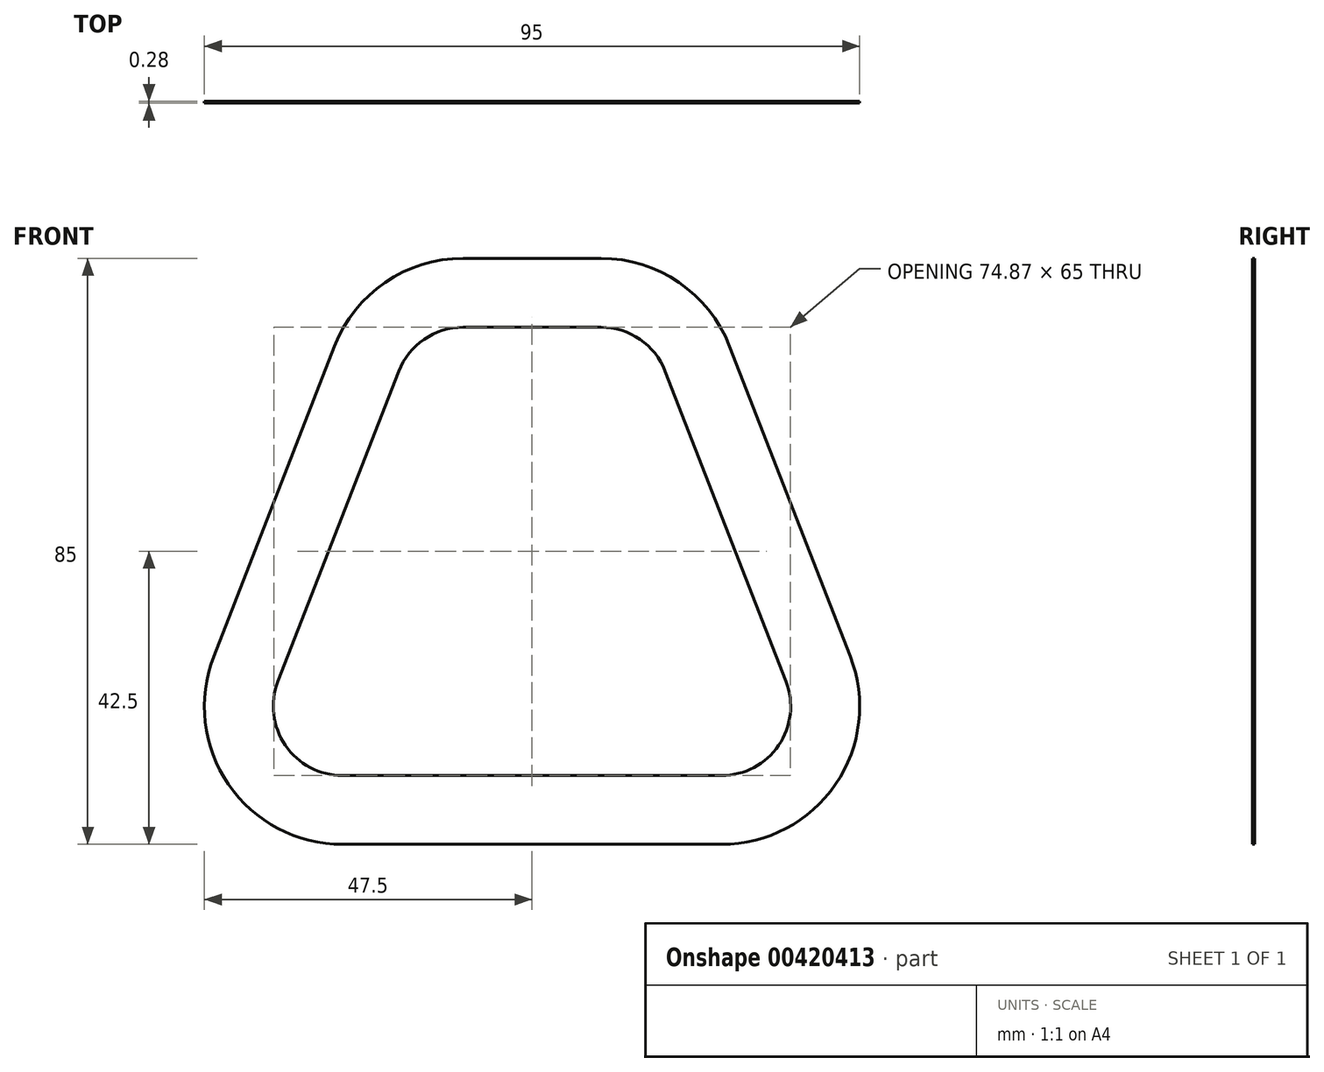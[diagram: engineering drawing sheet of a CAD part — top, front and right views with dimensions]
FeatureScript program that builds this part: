
annotation { "Feature Type Name" : "Feature", "Feature Type Description" : "" }
export const myFeature = defineFeature(function(context is Context, id is Id, definition is map)
    precondition{}
    {
        {
            var Q0;
            Q0=qCreatedBy(makeId("Front.planeOp"),FACE);
            var sketch = newSketch(context, id + "F0", { "sketchPlane" : qUnion([Q0])});
            skLineSegment(sketch, "E0", {"start": v(0, 0) * mm, "end": v(0, 20) * mm, "construction": true});
            skLineSegment(sketch, "E1", {"start": v(0, 20) * mm, "end": v(10, 20) * mm});
            skLineSegment(sketch, "E2", {"start": v(10, 20) * mm, "end": v(27.5, -25) * mm});
            skLineSegment(sketch, "E3", {"start": v(27.5, -25) * mm, "end": v(6.93, -25) * mm});
            skLineSegment(sketch, "E4", {"start": v(6.93, -25) * mm, "end": v(0, -13) * mm});
            skLineSegment(sketch, "E5", {"start": v(27.5, -25) * mm, "end": v(27.5, 20) * mm, "construction": true});
            skLineSegment(sketch, "E6", {"start": v(6.93, -25) * mm, "end": v(6.93, -13) * mm, "construction": true});
            skPoint(sketch, "E7.visualSharp", {"position": v(10, 20) * mm});
            skPoint(sketch, "E8.visualSharp", {"position": v(27.5, -25) * mm});
            skLineSegment(sketch, "E9.MirrorCS", {"start": v(0, 20) * mm, "end": v(-10, 20) * mm});
            skPoint(sketch, "E10.MirrorP", {"position": v(-27.5, -25) * mm});
            skLineSegment(sketch, "E11.MirrorCS", {"start": v(-10, 20) * mm, "end": v(-27.5, -25) * mm});
            skLineSegment(sketch, "E12.MirrorCS", {"start": v(-27.5, -25) * mm, "end": v(-6.93, -25) * mm});
            skLineSegment(sketch, "E13.MirrorCS", {"start": v(-27.5, -25) * mm, "end": v(-27.5, 20) * mm, "construction": true});
            skLineSegment(sketch, "E14.MirrorCS", {"start": v(-6.93, -25) * mm, "end": v(0, -13) * mm});
            skLineSegment(sketch, "E15.MirrorCS", {"start": v(-6.93, -25) * mm, "end": v(-6.93, -13) * mm, "construction": true});
            skLineSegment(sketch, "E16.0", {"start": v(0, 30) * mm, "end": v(10, 30) * mm});
            skLineSegment(sketch, "E16.1", {"start": v(0, 30) * mm, "end": v(-10, 30) * mm});
            skLineSegment(sketch, "E16.2", {"start": v(19.32, 23.62) * mm, "end": v(36.82, -21.38) * mm});
            skLineSegment(sketch, "E16.3", {"start": v(-19.32, 23.62) * mm, "end": v(-36.82, -21.38) * mm});
            skLineSegment(sketch, "E16.7", {"start": v(-27.5, -35) * mm, "end": v(27.5, -35) * mm});
            skLineSegment(sketch, "E17.0", {"start": v(-27.5, -45) * mm, "end": v(27.5, -45) * mm});
            skLineSegment(sketch, "E17.1", {"start": v(-28.64, 27.25) * mm, "end": v(-46.14, -17.75) * mm});
            skLineSegment(sketch, "E17.2", {"start": v(28.64, 27.25) * mm, "end": v(46.14, -17.75) * mm});
            skLineSegment(sketch, "E17.3", {"start": v(0, 40) * mm, "end": v(10, 40) * mm});
            skLineSegment(sketch, "E17.4", {"start": v(0, 40) * mm, "end": v(-10, 40) * mm});
            skPoint(sketch, "E18.visualSharp", {"position": v(-23.68, 40) * mm});
            skArc(sketch, "E18.filletArc", {"start": v(-10, 40) * mm, "mid": v(-21.3, 36.5) * mm, "end": v(-28.64, 27.25) * mm});
            skPoint(sketch, "E19.visualSharp", {"position": v(23.68, 40) * mm});
            skArc(sketch, "E19.filletArc", {"start": v(28.64, 27.25) * mm, "mid": v(21.3, 36.5) * mm, "end": v(10, 40) * mm});
            skPoint(sketch, "E20.visualSharp", {"position": v(56.74, -45) * mm});
            skArc(sketch, "E20.filletArc", {"start": v(27.5, -45) * mm, "mid": v(44, -36.3) * mm, "end": v(46.14, -17.75) * mm});
            skPoint(sketch, "E21.visualSharp", {"position": v(-56.74, -45) * mm});
            skArc(sketch, "E21.filletArc", {"start": v(-46.14, -17.75) * mm, "mid": v(-44, -36.3) * mm, "end": v(-27.5, -45) * mm});
            skPoint(sketch, "E22.visualSharp", {"position": v(-42.12, -35) * mm});
            skArc(sketch, "E22.filletArc", {"start": v(-36.82, -21.38) * mm, "mid": v(-35.75, -30.65) * mm, "end": v(-27.5, -35) * mm});
            skPoint(sketch, "E23.visualSharp", {"position": v(42.12, -35) * mm});
            skArc(sketch, "E23.filletArc", {"start": v(27.5, -35) * mm, "mid": v(35.75, -30.65) * mm, "end": v(36.82, -21.38) * mm});
            skPoint(sketch, "E24.visualSharp", {"position": v(16.84, 30) * mm});
            skArc(sketch, "E24.filletArc", {"start": v(19.32, 23.62) * mm, "mid": v(15.65, 28.25) * mm, "end": v(10, 30) * mm});
            skPoint(sketch, "E25.visualSharp", {"position": v(-16.84, 30) * mm});
            skArc(sketch, "E25.filletArc", {"start": v(-10, 30) * mm, "mid": v(-15.65, 28.25) * mm, "end": v(-19.32, 23.62) * mm});
            skSolve(sketch);
        }
        {
            var Q0;
            Q0=qSketchRegion(id+"F0",true);
            extrude(context, id + "F1", {"entities" : qUnion([Q0]), "depth" : (0.45 / 1.6) * mm});
        }
    });
